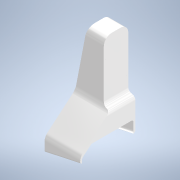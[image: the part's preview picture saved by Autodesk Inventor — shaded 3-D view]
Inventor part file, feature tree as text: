
AUTODESK INVENTOR PART (.ipt)
format: ipt  version: 2021 (Build 250183000, 183)  size: 294,912 bytes
history: native  units: mm
features: sketch x10, extrude x9, fillet x4, shell x1, hole x1
ambient origin geometry x8: Origin, YZ Plane, XZ Plane, XY Plane, X Axis, Y Axis, Z Axis, Center Point
bodies: Solid1 (feature_tree)
feature tree (25):
  extrude  "Extrusion1"  Depth=900.0mm
  extrude  "Extrusion2"  Depth=450.0mm
  extrude  "Extrusion3"  Depth=1500.0mm
  fillet  "Fillet5"  Radius=430.0mm
  fillet  "Fillet6"  Radius=180.0mm
  extrude  "Extrusion7"  Depth=100.0mm
  fillet  "Fillet7"  Radius=1000.0mm
  shell  "Shell2"  Thickness=100.0mm
  extrude  "Extrusion8"  Depth=2.094395mm
  extrude  "Extrusion9"  Depth=50.0mm TaperAngle=0.0deg
  fillet  "Fillet8"  Radius=50.0mm
  hole  "Hole1"  [1 undecoded]
  extrude  "Extrusion10"  Depth=6.0mm
  extrude  "Extrusion11"  Depth=200.0mm
  extrude  "Extrusion13"  Depth=50.0mm
  sketch  "Sketch1"  dims[d0=900.0mm d1=1400.0mm]
  sketch  "Sketch8"  dims[d2=700.0mm d3=450.0mm]
  sketch  "Sketch9"  dims[d4=1000.0mm d5=0.0mm d6=1500.0mm d7=430.0mm d8=180.0mm]
  sketch  "Sketch16"  dims[d9=620.0mm d10=0.0mm d11=6.981317mm d12=1000.0mm d13=0.0mm d28=100.0mm]
  sketch  "Sketch18"  dims[d29=200.0mm d30=2.094395mm]
  sketch  "Sketch19"  dims[d31=1100.0mm d32=1500.0mm d33=0.0mm d34=50.0mm]
  sketch  "Sketch20"  dims[d35=2.0mm d39=50.0mm]
  sketch  "Sketch21"  dims[d40=50.0mm d41=6.0mm]
  sketch  "Sketch22"  dims[d42=300.0mm d43=0.0mm d44=200.0mm]
  sketch  "Sketch24"  dims[d45=300.0mm d46=0.0mm d47=50.0mm d48=210.0mm d49=460.0mm d50=10.0mm d51=6.0mm d52=4.0mm d53=2.0mm d54=90.0deg d55=8.0mm d56=20.594885mm d57=6.981317mm d64=10.0mm d65=10.0mm d66=10.0mm d68=12.0mm d69=0.0mm d71=817.0mm d75=40.0mm d76=400.0mm d77=0.0mm d80=2.0mm d81=0.0mm]
note: 1 required parameter value undecoded (feature->parameter linkage not recoverable at this tier; creation-order binding heuristic only, values carry confidence <= 0.55)
